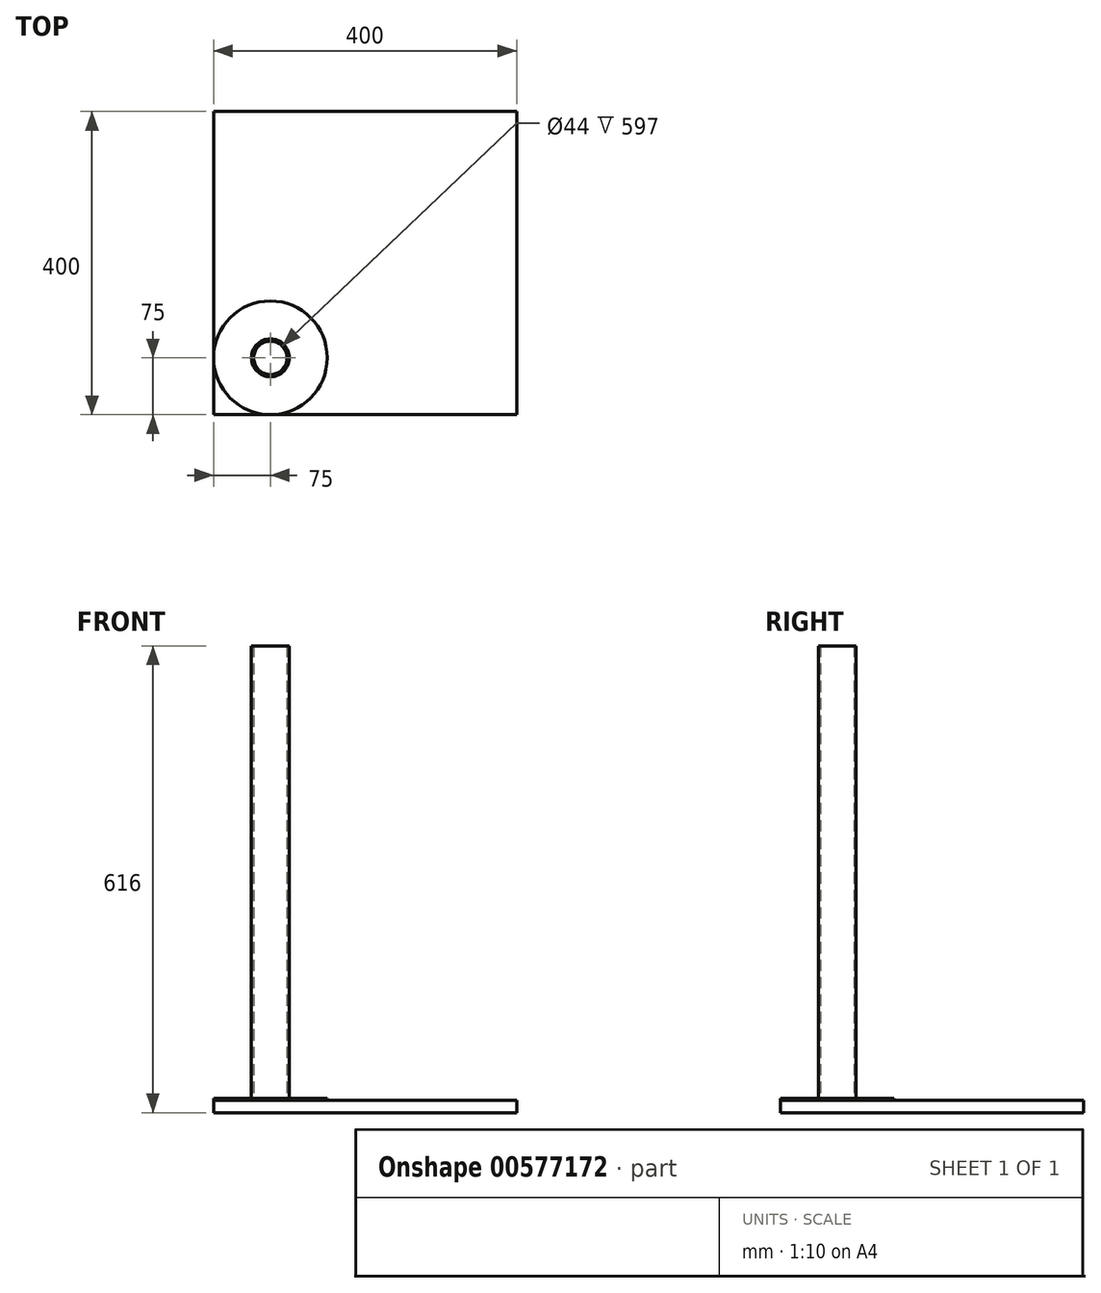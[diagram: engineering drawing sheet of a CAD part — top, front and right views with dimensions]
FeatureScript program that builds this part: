
annotation { "Feature Type Name" : "Feature", "Feature Type Description" : "" }
export const myFeature = defineFeature(function(context is Context, id is Id, definition is map)
    precondition{}
    {
        {
            var Q0;
            Q0=qCreatedBy(makeId("Top.planeOp"),FACE);
            var sketch = newSketch(context, id + "F0", { "sketchPlane" : qUnion([Q0])});
            skCircle(sketch, "E0", {"center": v(0, 0) * mm, "radius": 25 * mm});
            skSolve(sketch);
        }
        {
            var Q0;
            Q0=makeQuery(id+"F0.imprint","IMPRINT",FACE,{"disambiguationData":[TD([[makeQuery(id+"F0.imprint","IMPRINT",EDGE,{"derivedFrom":sQuery(id+"F0.wireOp",EDGE,"E0")}),1.0]])]});
            extrude(context, id + "F1", {"entities" : qUnion([Q0]), "depth" : 600 * mm, "offsetDistance" : 25 * mm});
        }
        {
            var Q0;
            Q0=makeQuery(id+"F1.opExtrude","CAP_FACE",FACE,{"disambiguationData":[OSD([sQuery(id+"F0.wireOp",EDGE,"E0")])],"isStart":false});
            var Q1;
            Q1=makeQuery(id+"F1.opExtrude","CAP_FACE",FACE,{"disambiguationData":[OSD([sQuery(id+"F0.wireOp",EDGE,"E0")])],"isStart":true});
            shell(context, id + "F2", {"entities" : qUnion([Q0, Q1]), "thickness" : 3 * mm});
        }
        {
            var Q0;
            Q0=qCreatedBy(makeId("Top.planeOp"),FACE);
            var sketch = newSketch(context, id + "F3", { "sketchPlane" : qUnion([Q0])});
            skCircle(sketch, "E1", {"center": v(0, 0) * mm, "radius": 75 * mm});
            skSolve(sketch);
        }
        {
            var Q0;
            Q0=makeQuery(id+"F3.imprint","IMPRINT",FACE,{"disambiguationData":[TD([[makeQuery(id+"F3.imprint","IMPRINT",EDGE,{"derivedFrom":sQuery(id+"F3.wireOp",EDGE,"E1")}),1.0]])]});
            extrude(context, id + "F4", {"entities" : qUnion([Q0]), "operationType" : NewBodyOperationType.ADD, "depth" : 3 * mm, "offsetDistance" : 25 * mm});
        }
        {
            var Q0;
            Q0=qCreatedBy(makeId("Top.planeOp"),FACE);
            var sketch = newSketch(context, id + "F5", { "sketchPlane" : qUnion([Q0])});
            skPoint(sketch, "E2.middle", {"position": v(0, 0) * mm});
            skLineSegment(sketch, "E3.bottom", {"start": v(-75, -75) * mm, "end": v(325, -75) * mm});
            skLineSegment(sketch, "E3.top", {"start": v(-75, 325) * mm, "end": v(325, 325) * mm});
            skLineSegment(sketch, "E3.left", {"start": v(-75, -75) * mm, "end": v(-75, 325) * mm});
            skLineSegment(sketch, "E3.right", {"start": v(325, -75) * mm, "end": v(325, 325) * mm});
            skSolve(sketch);
        }
        {
            var Q0;
            Q0=makeQuery(id+"F5.imprint","IMPRINT",FACE,{"disambiguationData":[TD([[makeQuery(id+"F5.imprint","IMPRINT",EDGE,{"derivedFrom":sQuery(id+"F5.wireOp",EDGE,"E2.bottom")}),1.0]])]});
            var Q1;
            Q1=makeQuery(id+"F5.imprint","IMPRINT",FACE,{"disambiguationData":[TD([[makeQuery(id+"F5.imprint","IMPRINT",EDGE,{"derivedFrom":sQuery(id+"F5.wireOp",EDGE,"E3.bottom")}),1.0]])]});
            extrude(context, id + "F6", {"entities" : qUnion([Q0, Q1]), "operationType" : NewBodyOperationType.ADD, "oppositeDirection" : true, "depth" : 16 * mm, "offsetDistance" : 25 * mm});
        }
    });
